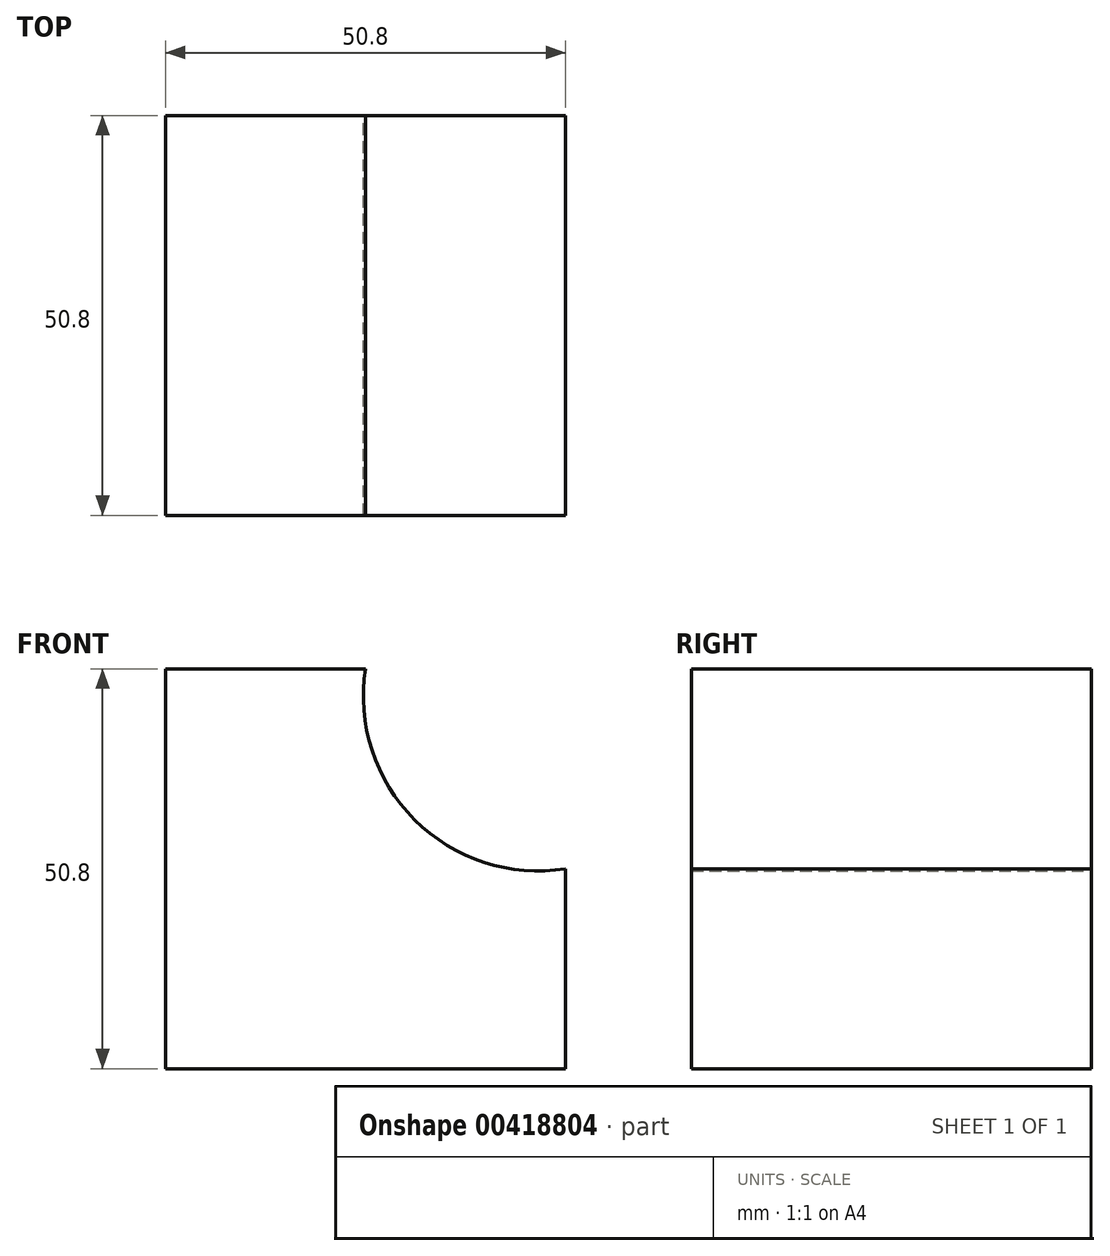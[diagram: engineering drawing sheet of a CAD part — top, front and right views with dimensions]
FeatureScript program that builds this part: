
annotation { "Feature Type Name" : "Feature", "Feature Type Description" : "" }
export const myFeature = defineFeature(function(context is Context, id is Id, definition is map)
    precondition{}
    {
        {
            var Q0;
            Q0=qCreatedBy(makeId("Front.planeOp"),FACE);
            var sketch = newSketch(context, id + "F0", { "sketchPlane" : qUnion([Q0])});
            skLineSegment(sketch, "E0", {"start": v(-16.42, 54.43) * mm, "end": v(-41.82, 54.43) * mm});
            skLineSegment(sketch, "E1", {"start": v(-41.82, 54.43) * mm, "end": v(-41.82, 3.63) * mm});
            skLineSegment(sketch, "E2", {"start": v(-41.82, 3.63) * mm, "end": v(8.98, 3.63) * mm});
            skLineSegment(sketch, "E3", {"start": v(8.98, 3.63) * mm, "end": v(8.98, 29.03) * mm});
            skArc(sketch, "E4", {"start": v(-16.42, 54.43) * mm, "mid": v(-10.2, 35.26) * mm, "end": v(8.98, 29.03) * mm});
            skSolve(sketch);
        }
        {
            var Q0;
            Q0=makeQuery(id+"F0.imprint","IMPRINT",FACE,{"disambiguationData":[TD([[makeQuery(id+"F0.imprint","IMPRINT",EDGE,{"derivedFrom":sQuery(id+"F0.wireOp",EDGE,"E0")}),1.0]])]});
            extrude(context, id + "F1", {"entities" : qUnion([Q0]), "depth" : 50.8 * mm});
        }
    });
